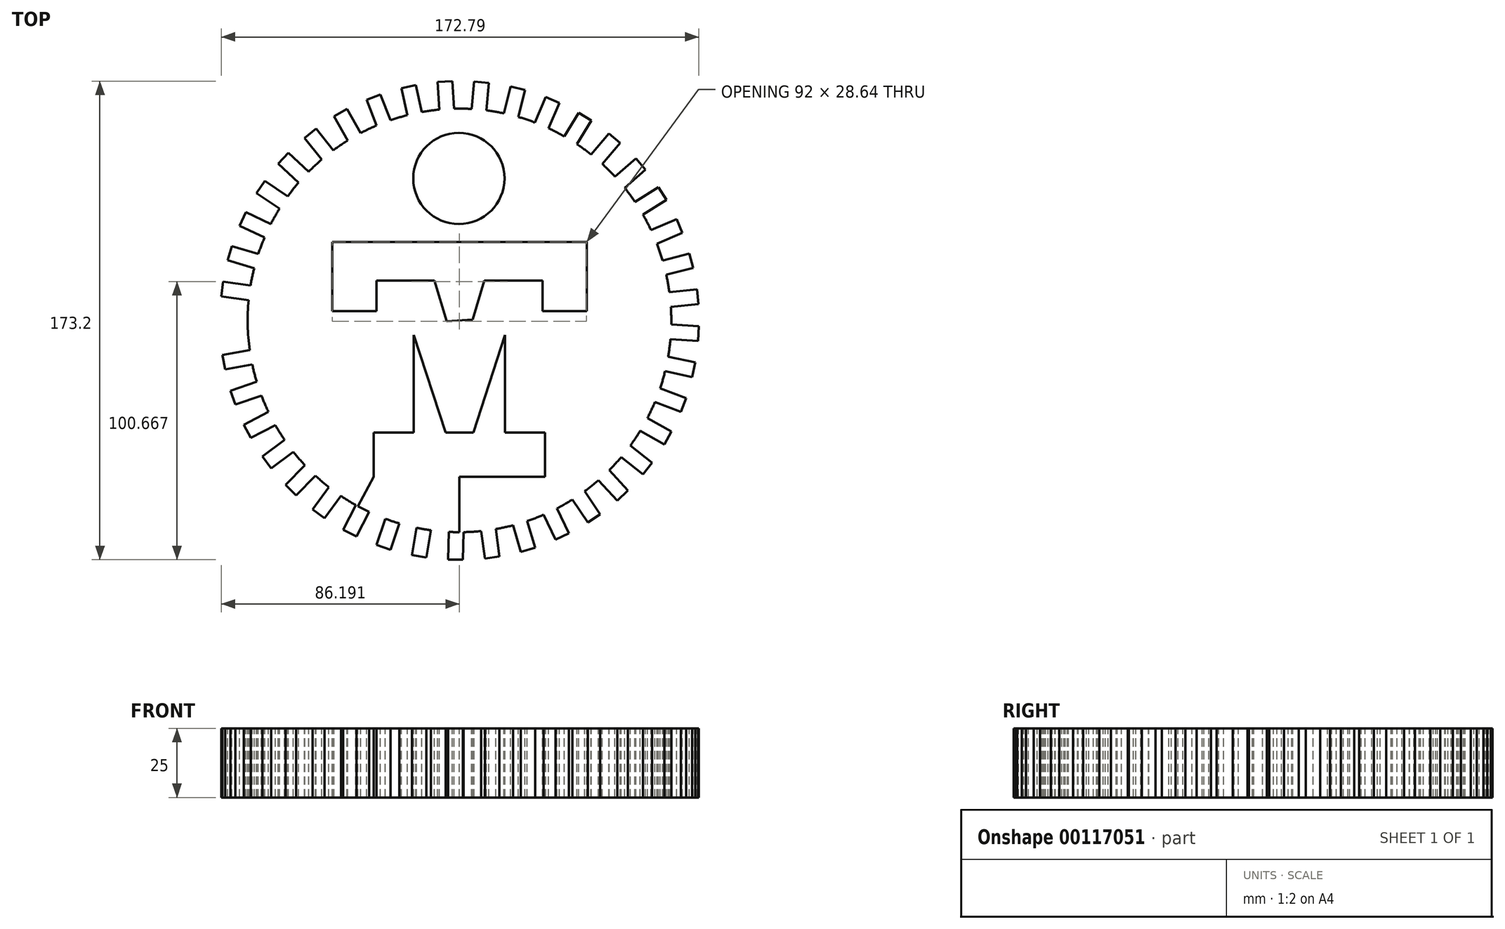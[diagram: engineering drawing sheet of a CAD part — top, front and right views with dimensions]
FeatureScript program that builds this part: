
annotation { "Feature Type Name" : "Feature", "Feature Type Description" : "" }
export const myFeature = defineFeature(function(context is Context, id is Id, definition is map)
    precondition{}
    {
        {
            var Q0;
            Q0=qCreatedBy(makeId("Top.planeOp"),FACE);
            var sketch = newSketch(context, id + "F0", { "sketchPlane" : qUnion([Q0])});
            skLineSegment(sketch, "E0", {"start": v(-32.27, 42.96) * mm, "end": v(-32.27, 17.96) * mm});
            skLineSegment(sketch, "E1", {"start": v(-32.27, 42.96) * mm, "end": v(59.73, 42.96) * mm});
            skLineSegment(sketch, "E2", {"start": v(59.73, 42.96) * mm, "end": v(59.73, 17.96) * mm});
            skLineSegment(sketch, "E3", {"start": v(59.73, 17.96) * mm, "end": v(43.73, 17.96) * mm});
            skLineSegment(sketch, "E4", {"start": v(43.73, 17.96) * mm, "end": v(43.73, 28.96) * mm});
            skLineSegment(sketch, "E5", {"start": v(43.73, 28.96) * mm, "end": v(22.73, 28.96) * mm});
            skLineSegment(sketch, "E6", {"start": v(22.73, 28.96) * mm, "end": v(13.73, -1.04) * mm});
            skLineSegment(sketch, "E7", {"start": v(13.73, -1.04) * mm, "end": v(4.73, 28.96) * mm});
            skLineSegment(sketch, "E8", {"start": v(4.73, 28.96) * mm, "end": v(-16.27, 28.96) * mm});
            skLineSegment(sketch, "E9", {"start": v(-16.27, 28.96) * mm, "end": v(-16.27, 17.96) * mm});
            skLineSegment(sketch, "E10", {"start": v(-16.27, 17.96) * mm, "end": v(-32.27, 17.96) * mm});
            skLineSegment(sketch, "E11", {"start": v(-2.77, 9.26) * mm, "end": v(-2.77, -26.04) * mm});
            skLineSegment(sketch, "E12", {"start": v(-2.77, -26.04) * mm, "end": v(-17.27, -26.04) * mm});
            skLineSegment(sketch, "E13", {"start": v(-17.27, -26.04) * mm, "end": v(-17.27, -42.04) * mm});
            skLineSegment(sketch, "E14", {"start": v(-17.27, -42.04) * mm, "end": v(44.73, -42.04) * mm});
            skLineSegment(sketch, "E15", {"start": v(44.73, -42.04) * mm, "end": v(44.73, -26.04) * mm});
            skLineSegment(sketch, "E16", {"start": v(44.73, -26.04) * mm, "end": v(30.23, -26.04) * mm});
            skLineSegment(sketch, "E17", {"start": v(30.23, -26.04) * mm, "end": v(30.23, 9.26) * mm});
            skLineSegment(sketch, "E18", {"start": v(30.23, 9.26) * mm, "end": v(18.73, -26.04) * mm});
            skLineSegment(sketch, "E19", {"start": v(18.73, -26.04) * mm, "end": v(8.73, -26.04) * mm});
            skLineSegment(sketch, "E20", {"start": v(8.73, -26.04) * mm, "end": v(-2.77, 9.26) * mm});
            skCircle(sketch, "E21", {"center": v(13.52, 65.96) * mm, "radius": 16.5 * mm});
            skLineSegment(sketch, "E22", {"start": v(13.73, -1.04) * mm, "end": v(13.73, -42.04) * mm});
            skCircle(sketch, "E23", {"center": v(13.73, 14.58) * mm, "radius": 76.63 * mm});
            skLineSegment(sketch, "E24", {"start": v(13.73, 14.58) * mm, "end": v(13.73, 42.96) * mm});
            skPoint(sketch, "E24.endSnap0", {"position": v(13.73, 42.96) * mm});
            skLineSegment(sketch, "E25", {"start": v(13.73, -62.04) * mm, "end": v(13.73, -42.04) * mm});
            skPoint(sketch, "E26", {"position": v(-62.74, 19.53) * mm});
            skPoint(sketch, "E27", {"position": v(-62.08, 3.44) * mm});
            skLineSegment(sketch, "E28", {"start": v(13.73, 14.58) * mm, "end": v(9.12, 14.32) * mm});
            skLineSegment(sketch, "E29", {"start": v(-62.77, 10.21) * mm, "end": v(-72.77, 10) * mm});
            skLineSegment(sketch, "E30", {"start": v(-72.77, 10) * mm, "end": v(-72.89, 15.34) * mm});
            skLineSegment(sketch, "E31", {"start": v(-72.89, 15.34) * mm, "end": v(-62.89, 15.56) * mm});
            skLineSegment(sketch, "E32", {"start": v(-62.89, 15.56) * mm, "end": v(-62.77, 10.21) * mm});
            skLineSegment(sketch, "E33.1.0", {"start": v(-72.46, 23.25) * mm, "end": v(-71.76, 28.55) * mm});
            skLineSegment(sketch, "E33.1.1", {"start": v(-71.76, 28.55) * mm, "end": v(-61.84, 27.24) * mm});
            skLineSegment(sketch, "E33.1.2", {"start": v(-62.54, 21.94) * mm, "end": v(-72.46, 23.25) * mm});
            skPoint(sketch, "E33.1.3", {"position": v(-62.9, 15.15) * mm});
            skLineSegment(sketch, "E33.2.0", {"start": v(-70.13, 36.3) * mm, "end": v(-68.63, 41.44) * mm});
            skLineSegment(sketch, "E33.2.1", {"start": v(-68.63, 41.44) * mm, "end": v(-59.02, 38.63) * mm});
            skLineSegment(sketch, "E33.2.2", {"start": v(-60.52, 33.5) * mm, "end": v(-70.13, 36.3) * mm});
            skPoint(sketch, "E33.2.3", {"position": v(-61.91, 26.84) * mm});
            skLineSegment(sketch, "E33.3.0", {"start": v(-65.83, 48.85) * mm, "end": v(-63.56, 53.7) * mm});
            skLineSegment(sketch, "E33.3.1", {"start": v(-63.56, 53.7) * mm, "end": v(-54.5, 49.46) * mm});
            skLineSegment(sketch, "E33.3.2", {"start": v(-56.77, 44.61) * mm, "end": v(-65.83, 48.85) * mm});
            skPoint(sketch, "E33.3.3", {"position": v(-59.15, 38.24) * mm});
            skLineSegment(sketch, "E33.4.0", {"start": v(-59.66, 60.6) * mm, "end": v(-56.68, 65.04) * mm});
            skLineSegment(sketch, "E33.4.1", {"start": v(-56.68, 65.04) * mm, "end": v(-48.38, 59.46) * mm});
            skLineSegment(sketch, "E33.4.2", {"start": v(-51.36, 55.02) * mm, "end": v(-59.66, 60.6) * mm});
            skPoint(sketch, "E33.4.3", {"position": v(-54.69, 49.09) * mm});
            skLineSegment(sketch, "E33.5.0", {"start": v(-51.78, 71.26) * mm, "end": v(-48.16, 75.2) * mm});
            skLineSegment(sketch, "E33.5.1", {"start": v(-48.16, 75.2) * mm, "end": v(-40.8, 68.42) * mm});
            skLineSegment(sketch, "E33.5.2", {"start": v(-44.42, 64.48) * mm, "end": v(-51.78, 71.26) * mm});
            skPoint(sketch, "E33.5.3", {"position": v(-48.62, 59.13) * mm});
            skLineSegment(sketch, "E33.6.0", {"start": v(-42.36, 80.6) * mm, "end": v(-38.18, 83.93) * mm});
            skLineSegment(sketch, "E33.6.1", {"start": v(-38.18, 83.93) * mm, "end": v(-31.94, 76.11) * mm});
            skLineSegment(sketch, "E33.6.2", {"start": v(-36.12, 72.78) * mm, "end": v(-42.36, 80.6) * mm});
            skPoint(sketch, "E33.6.3", {"position": v(-41.09, 68.12) * mm});
            skLineSegment(sketch, "E33.7.0", {"start": v(-31.63, 88.38) * mm, "end": v(-26.99, 91.04) * mm});
            skLineSegment(sketch, "E33.7.1", {"start": v(-26.99, 91.04) * mm, "end": v(-22.01, 82.36) * mm});
            skLineSegment(sketch, "E33.7.2", {"start": v(-26.65, 79.7) * mm, "end": v(-31.63, 88.38) * mm});
            skPoint(sketch, "E33.7.3", {"position": v(-32.27, 75.86) * mm});
            skLineSegment(sketch, "E33.8.0", {"start": v(-19.83, 94.44) * mm, "end": v(-14.84, 96.36) * mm});
            skLineSegment(sketch, "E33.8.1", {"start": v(-14.84, 96.36) * mm, "end": v(-11.25, 87.02) * mm});
            skLineSegment(sketch, "E33.8.2", {"start": v(-16.24, 85.1) * mm, "end": v(-19.83, 94.44) * mm});
            skPoint(sketch, "E33.8.3", {"position": v(-22.38, 82.17) * mm});
            skLineSegment(sketch, "E33.9.0", {"start": v(-7.25, 98.63) * mm, "end": v(-2.02, 99.76) * mm});
            skLineSegment(sketch, "E33.9.1", {"start": v(-2.02, 99.76) * mm, "end": v(0.1, 89.99) * mm});
            skLineSegment(sketch, "E33.9.2", {"start": v(-5.12, 88.85) * mm, "end": v(-7.25, 98.63) * mm});
            skPoint(sketch, "E33.9.3", {"position": v(-11.64, 86.89) * mm});
            skLineSegment(sketch, "E33.10.0", {"start": v(5.83, 100.85) * mm, "end": v(11.17, 101.17) * mm});
            skLineSegment(sketch, "E33.10.1", {"start": v(11.17, 101.17) * mm, "end": v(11.77, 91.18) * mm});
            skLineSegment(sketch, "E33.10.2", {"start": v(6.43, 90.86) * mm, "end": v(5.83, 100.85) * mm});
            skPoint(sketch, "E33.10.3", {"position": v(-0.3, 89.91) * mm});
            skLineSegment(sketch, "E33.11.0", {"start": v(19.1, 101.04) * mm, "end": v(24.42, 100.54) * mm});
            skLineSegment(sketch, "E33.11.1", {"start": v(24.42, 100.54) * mm, "end": v(23.49, 90.59) * mm});
            skLineSegment(sketch, "E33.11.2", {"start": v(18.16, 91.08) * mm, "end": v(19.1, 101.04) * mm});
            skPoint(sketch, "E33.11.3", {"position": v(11.36, 91.17) * mm});
            skLineSegment(sketch, "E33.12.0", {"start": v(32.23, 99.2) * mm, "end": v(37.41, 97.9) * mm});
            skLineSegment(sketch, "E33.12.1", {"start": v(37.41, 97.9) * mm, "end": v(34.98, 88.2) * mm});
            skLineSegment(sketch, "E33.12.2", {"start": v(29.79, 89.5) * mm, "end": v(32.23, 99.2) * mm});
            skPoint(sketch, "E33.12.3", {"position": v(23.08, 90.64) * mm});
            skLineSegment(sketch, "E33.13.0", {"start": v(44.93, 95.4) * mm, "end": v(49.85, 93.31) * mm});
            skLineSegment(sketch, "E33.13.1", {"start": v(49.85, 93.31) * mm, "end": v(45.97, 84.1) * mm});
            skLineSegment(sketch, "E33.13.2", {"start": v(41.04, 86.18) * mm, "end": v(44.93, 95.4) * mm});
            skPoint(sketch, "E33.13.3", {"position": v(34.58, 88.32) * mm});
            skLineSegment(sketch, "E33.14.0", {"start": v(56.9, 89.69) * mm, "end": v(61.45, 86.88) * mm});
            skLineSegment(sketch, "E33.14.1", {"start": v(61.45, 86.88) * mm, "end": v(56.2, 78.36) * mm});
            skLineSegment(sketch, "E33.14.2", {"start": v(51.65, 81.17) * mm, "end": v(56.9, 89.69) * mm});
            skPoint(sketch, "E33.14.3", {"position": v(45.6, 84.27) * mm});
            skLineSegment(sketch, "E33.15.0", {"start": v(67.86, 82.22) * mm, "end": v(71.93, 78.75) * mm});
            skLineSegment(sketch, "E33.15.1", {"start": v(71.93, 78.75) * mm, "end": v(65.44, 71.13) * mm});
            skLineSegment(sketch, "E33.15.2", {"start": v(61.37, 74.6) * mm, "end": v(67.86, 82.22) * mm});
            skPoint(sketch, "E33.15.3", {"position": v(55.86, 78.6) * mm});
            skLineSegment(sketch, "E33.16.0", {"start": v(77.55, 73.16) * mm, "end": v(81.04, 69.11) * mm});
            skLineSegment(sketch, "E33.16.1", {"start": v(81.04, 69.11) * mm, "end": v(73.46, 62.58) * mm});
            skLineSegment(sketch, "E33.16.2", {"start": v(69.97, 66.63) * mm, "end": v(77.55, 73.16) * mm});
            skPoint(sketch, "E33.16.3", {"position": v(65.13, 71.41) * mm});
            skLineSegment(sketch, "E33.17.0", {"start": v(85.74, 62.73) * mm, "end": v(88.57, 58.2) * mm});
            skLineSegment(sketch, "E33.17.1", {"start": v(88.57, 58.2) * mm, "end": v(80.1, 52.9) * mm});
            skLineSegment(sketch, "E33.17.2", {"start": v(77.26, 57.43) * mm, "end": v(85.74, 62.73) * mm});
            skPoint(sketch, "E33.17.3", {"position": v(73.2, 62.9) * mm});
            skLineSegment(sketch, "E33.18.0", {"start": v(92.25, 51.18) * mm, "end": v(94.35, 46.26) * mm});
            skLineSegment(sketch, "E33.18.1", {"start": v(94.35, 46.26) * mm, "end": v(85.16, 42.32) * mm});
            skLineSegment(sketch, "E33.18.2", {"start": v(83.05, 47.23) * mm, "end": v(92.25, 51.18) * mm});
            skPoint(sketch, "E33.18.3", {"position": v(79.88, 53.25) * mm});
            skLineSegment(sketch, "E33.19.0", {"start": v(96.91, 38.76) * mm, "end": v(98.25, 33.58) * mm});
            skLineSegment(sketch, "E33.19.1", {"start": v(98.25, 33.58) * mm, "end": v(88.56, 31.09) * mm});
            skLineSegment(sketch, "E33.19.2", {"start": v(87.23, 36.27) * mm, "end": v(96.91, 38.76) * mm});
            skPoint(sketch, "E33.19.3", {"position": v(85.01, 42.7) * mm});
            skLineSegment(sketch, "E33.20.0", {"start": v(99.63, 25.78) * mm, "end": v(100.16, 20.46) * mm});
            skLineSegment(sketch, "E33.20.1", {"start": v(100.16, 20.46) * mm, "end": v(90.2, 19.47) * mm});
            skLineSegment(sketch, "E33.20.2", {"start": v(89.67, 24.8) * mm, "end": v(99.63, 25.78) * mm});
            skPoint(sketch, "E33.20.3", {"position": v(88.47, 31.5) * mm});
            skLineSegment(sketch, "E33.21.0", {"start": v(100.33, 12.54) * mm, "end": v(100.04, 7.2) * mm});
            skLineSegment(sketch, "E33.21.1", {"start": v(100.04, 7.2) * mm, "end": v(90.05, 7.74) * mm});
            skLineSegment(sketch, "E33.21.2", {"start": v(90.34, 13.08) * mm, "end": v(100.33, 12.54) * mm});
            skPoint(sketch, "E33.21.3", {"position": v(90.17, 19.89) * mm});
            skLineSegment(sketch, "E33.22.0", {"start": v(99, -0.66) * mm, "end": v(97.9, -5.9) * mm});
            skLineSegment(sketch, "E33.22.1", {"start": v(97.9, -5.9) * mm, "end": v(88.11, -3.83) * mm});
            skLineSegment(sketch, "E33.22.2", {"start": v(89.22, 1.4) * mm, "end": v(99, -0.66) * mm});
            skPoint(sketch, "E33.22.3", {"position": v(90.09, 8.15) * mm});
            skLineSegment(sketch, "E33.23.0", {"start": v(95.68, -13.5) * mm, "end": v(93.79, -18.5) * mm});
            skLineSegment(sketch, "E33.23.1", {"start": v(93.79, -18.5) * mm, "end": v(84.43, -14.97) * mm});
            skLineSegment(sketch, "E33.23.2", {"start": v(86.32, -9.96) * mm, "end": v(95.68, -13.5) * mm});
            skPoint(sketch, "E33.23.3", {"position": v(88.21, -3.43) * mm});
            skLineSegment(sketch, "E33.24.0", {"start": v(90.43, -25.68) * mm, "end": v(87.8, -30.33) * mm});
            skLineSegment(sketch, "E33.24.1", {"start": v(87.8, -30.33) * mm, "end": v(79.1, -25.41) * mm});
            skLineSegment(sketch, "E33.24.2", {"start": v(81.72, -20.76) * mm, "end": v(90.43, -25.68) * mm});
            skPoint(sketch, "E33.24.3", {"position": v(84.59, -14.58) * mm});
            skLineSegment(sketch, "E33.25.0", {"start": v(83.39, -36.91) * mm, "end": v(80.08, -41.11) * mm});
            skLineSegment(sketch, "E33.25.1", {"start": v(80.08, -41.11) * mm, "end": v(72.22, -34.92) * mm});
            skLineSegment(sketch, "E33.25.2", {"start": v(75.53, -30.72) * mm, "end": v(83.39, -36.91) * mm});
            skPoint(sketch, "E33.25.3", {"position": v(79.3, -25.06) * mm});
            skLineSegment(sketch, "E33.26.0", {"start": v(74.71, -46.94) * mm, "end": v(70.8, -50.59) * mm});
            skLineSegment(sketch, "E33.26.1", {"start": v(70.8, -50.59) * mm, "end": v(63.98, -43.27) * mm});
            skLineSegment(sketch, "E33.26.2", {"start": v(67.9, -39.62) * mm, "end": v(74.71, -46.94) * mm});
            skPoint(sketch, "E33.26.3", {"position": v(72.49, -34.6) * mm});
            skLineSegment(sketch, "E33.27.0", {"start": v(64.6, -55.53) * mm, "end": v(60.18, -58.54) * mm});
            skLineSegment(sketch, "E33.27.1", {"start": v(60.18, -58.54) * mm, "end": v(54.56, -50.26) * mm});
            skLineSegment(sketch, "E33.27.2", {"start": v(58.98, -47.26) * mm, "end": v(64.6, -55.53) * mm});
            skPoint(sketch, "E33.27.3", {"position": v(64.3, -43) * mm});
            skLineSegment(sketch, "E33.28.0", {"start": v(53.3, -62.47) * mm, "end": v(48.48, -64.77) * mm});
            skLineSegment(sketch, "E33.28.1", {"start": v(48.48, -64.77) * mm, "end": v(44.18, -55.73) * mm});
            skLineSegment(sketch, "E33.28.2", {"start": v(49.01, -53.44) * mm, "end": v(53.3, -62.47) * mm});
            skPoint(sketch, "E33.28.3", {"position": v(54.9, -50.04) * mm});
            skLineSegment(sketch, "E33.29.0", {"start": v(41.08, -67.61) * mm, "end": v(35.95, -69.14) * mm});
            skLineSegment(sketch, "E33.29.1", {"start": v(35.95, -69.14) * mm, "end": v(33.1, -59.56) * mm});
            skLineSegment(sketch, "E33.29.2", {"start": v(38.22, -58.03) * mm, "end": v(41.08, -67.61) * mm});
            skPoint(sketch, "E33.29.3", {"position": v(44.56, -55.57) * mm});
            skLineSegment(sketch, "E33.30.0", {"start": v(28.21, -70.82) * mm, "end": v(22.91, -71.55) * mm});
            skLineSegment(sketch, "E33.30.1", {"start": v(22.91, -71.55) * mm, "end": v(21.55, -61.65) * mm});
            skLineSegment(sketch, "E33.30.2", {"start": v(26.85, -60.91) * mm, "end": v(28.21, -70.82) * mm});
            skPoint(sketch, "E33.30.3", {"position": v(33.5, -59.45) * mm});
            skLineSegment(sketch, "E33.31.0", {"start": v(15, -72.03) * mm, "end": v(9.66, -71.95) * mm});
            skLineSegment(sketch, "E33.31.1", {"start": v(9.66, -71.95) * mm, "end": v(9.82, -61.94) * mm});
            skLineSegment(sketch, "E33.31.2", {"start": v(15.17, -62.03) * mm, "end": v(15, -72.03) * mm});
            skPoint(sketch, "E33.31.3", {"position": v(21.96, -61.6) * mm});
            skLineSegment(sketch, "E33.32.0", {"start": v(1.77, -71.21) * mm, "end": v(-3.5, -70.31) * mm});
            skLineSegment(sketch, "E33.32.1", {"start": v(-3.5, -70.31) * mm, "end": v(-1.82, -60.45) * mm});
            skLineSegment(sketch, "E33.32.2", {"start": v(3.46, -61.35) * mm, "end": v(1.77, -71.21) * mm});
            skPoint(sketch, "E33.32.3", {"position": v(10.23, -61.96) * mm});
            skLineSegment(sketch, "E33.33.0", {"start": v(-11.19, -68.38) * mm, "end": v(-16.26, -66.68) * mm});
            skLineSegment(sketch, "E33.33.1", {"start": v(-16.26, -66.68) * mm, "end": v(-13.09, -57.2) * mm});
            skLineSegment(sketch, "E33.33.2", {"start": v(-8.02, -58.9) * mm, "end": v(-11.19, -68.38) * mm});
            skPoint(sketch, "E33.33.3", {"position": v(-1.41, -60.53) * mm});
            skLineSegment(sketch, "E33.34.0", {"start": v(-23.56, -63.6) * mm, "end": v(-28.31, -61.15) * mm});
            skLineSegment(sketch, "E33.34.1", {"start": v(-28.31, -61.15) * mm, "end": v(-23.73, -52.26) * mm});
            skLineSegment(sketch, "E33.34.2", {"start": v(-18.98, -54.71) * mm, "end": v(-23.56, -63.6) * mm});
            skPoint(sketch, "E33.34.3", {"position": v(-12.7, -57.34) * mm});
            skLineSegment(sketch, "E33.35.0", {"start": v(-35.06, -57) * mm, "end": v(-39.38, -53.85) * mm});
            skLineSegment(sketch, "E33.35.1", {"start": v(-39.38, -53.85) * mm, "end": v(-33.5, -45.76) * mm});
            skLineSegment(sketch, "E33.35.2", {"start": v(-29.17, -48.9) * mm, "end": v(-35.06, -57) * mm});
            skPoint(sketch, "E33.35.3", {"position": v(-23.37, -52.46) * mm});
            skLineSegment(sketch, "E33.36.0", {"start": v(-45.41, -48.7) * mm, "end": v(-49.2, -44.94) * mm});
            skLineSegment(sketch, "E33.36.1", {"start": v(-49.2, -44.94) * mm, "end": v(-42.15, -37.84) * mm});
            skLineSegment(sketch, "E33.36.2", {"start": v(-38.36, -41.62) * mm, "end": v(-45.41, -48.7) * mm});
            skPoint(sketch, "E33.36.3", {"position": v(-33.17, -46.02) * mm});
            skLineSegment(sketch, "E33.37.0", {"start": v(-54.38, -38.94) * mm, "end": v(-57.55, -34.63) * mm});
            skLineSegment(sketch, "E33.37.1", {"start": v(-57.55, -34.63) * mm, "end": v(-49.5, -28.7) * mm});
            skLineSegment(sketch, "E33.37.2", {"start": v(-46.33, -33) * mm, "end": v(-54.38, -38.94) * mm});
            skPoint(sketch, "E33.37.3", {"position": v(-41.87, -38.15) * mm});
            skLineSegment(sketch, "E33.38.0", {"start": v(-61.75, -27.92) * mm, "end": v(-64.23, -23.18) * mm});
            skLineSegment(sketch, "E33.38.1", {"start": v(-64.23, -23.18) * mm, "end": v(-55.37, -18.54) * mm});
            skLineSegment(sketch, "E33.38.2", {"start": v(-52.89, -23.28) * mm, "end": v(-61.75, -27.92) * mm});
            skPoint(sketch, "E33.38.3", {"position": v(-49.27, -29.04) * mm});
            skLineSegment(sketch, "E33.39.0", {"start": v(-67.35, -15.9) * mm, "end": v(-69.08, -10.83) * mm});
            skLineSegment(sketch, "E33.39.1", {"start": v(-69.08, -10.83) * mm, "end": v(-59.61, -7.6) * mm});
            skLineSegment(sketch, "E33.39.2", {"start": v(-57.89, -12.67) * mm, "end": v(-67.35, -15.9) * mm});
            skPoint(sketch, "E33.39.3", {"position": v(-55.19, -18.91) * mm});
            skLineSegment(sketch, "E33.40.0", {"start": v(-71.06, -3.16) * mm, "end": v(-72, 2.1) * mm});
            skLineSegment(sketch, "E33.40.1", {"start": v(-72, 2.1) * mm, "end": v(-62.14, 3.85) * mm});
            skLineSegment(sketch, "E33.40.2", {"start": v(-61.2, -1.41) * mm, "end": v(-71.06, -3.16) * mm});
            skPoint(sketch, "E33.40.3", {"position": v(-59.5, -8) * mm});
            skLineSegment(sketch, "E33.anchor1", {"start": v(13.73, 14.58) * mm, "end": v(-72.77, 10) * mm, "construction": true});
            skLineSegment(sketch, "E33.anchor2", {"start": v(13.73, 14.58) * mm, "end": v(-72.77, 10) * mm, "construction": true});
            skLineSegment(sketch, "E34.trimOffspring", {"start": v(13.73, 49.46) * mm, "end": v(13.73, 82.45) * mm});
            skPoint(sketch, "E35.orphan", {"position": v(13.73, 91.2) * mm});
            skLineSegment(sketch, "E36.trimOffspring", {"start": v(72.78, 17.96) * mm, "end": v(-16.27, 12.87) * mm});
            skArc(sketch, "E37", {"start": v(-69.08, -10.83) * mm, "mid": v(-75.61, -6.16) * mm, "end": v(-82.15, -10.83) * mm});
            skLineSegment(sketch, "E38", {"start": v(-17.27, -42.04) * mm, "end": v(-23.07, -52.63) * mm});
            skLineSegment(sketch, "E39", {"start": v(13.73, 82.45) * mm, "end": v(13.73, 91.2) * mm});
            skSolve(sketch);
        }
        {
            var Q0;
            {var subQ81=sQuery(id+"F0.wireOp",EDGE,"E0");Q0=makeQuery(id+"F0.imprint","IMPRINT",FACE,{"disambiguationData":[TD([[makeQuery(id+"F0.imprint","IMPRINT",EDGE,{"derivedFrom":subQ81}),-1.0]])]});}
            var Q1;
            {var subQ3=sQuery(id+"F0.wireOp",EDGE,"E36.trimOffspring");Q1=makeQuery(id+"F0.imprint","IMPRINT",FACE,{"disambiguationData":[TD([[makeQuery(id+"F0.imprint","IMPRINT",EDGE,{"derivedFrom":subQ3}),1.0]])]});}
            var Q2;
            Q2=makeQuery(id+"F0.imprint","IMPRINT",FACE,{"disambiguationData":[TD([[makeQuery(id+"F0.imprint","IMPRINT",EDGE,{"derivedFrom":sQuery(id+"F0.wireOp",EDGE,"E33.35.0")}),-1.0]])]});
            var Q3;
            Q3=makeQuery(id+"F0.imprint","IMPRINT",FACE,{"disambiguationData":[TD([[makeQuery(id+"F0.imprint","IMPRINT",EDGE,{"derivedFrom":sQuery(id+"F0.wireOp",EDGE,"E33.33.0")}),-1.0]])]});
            var Q4;
            Q4=makeQuery(id+"F0.imprint","IMPRINT",FACE,{"disambiguationData":[TD([[makeQuery(id+"F0.imprint","IMPRINT",EDGE,{"derivedFrom":sQuery(id+"F0.wireOp",EDGE,"E33.6.0")}),-1.0]])]});
            var Q5;
            Q5=makeQuery(id+"F0.imprint","IMPRINT",FACE,{"disambiguationData":[TD([[makeQuery(id+"F0.imprint","IMPRINT",EDGE,{"derivedFrom":sQuery(id+"F0.wireOp",EDGE,"E33.19.0")}),-1.0]])]});
            var Q6;
            Q6=makeQuery(id+"F0.imprint","IMPRINT",FACE,{"disambiguationData":[TD([[makeQuery(id+"F0.imprint","IMPRINT",EDGE,{"derivedFrom":sQuery(id+"F0.wireOp",EDGE,"E33.18.0")}),-1.0]])]});
            var Q7;
            Q7=makeQuery(id+"F0.imprint","IMPRINT",FACE,{"disambiguationData":[TD([[makeQuery(id+"F0.imprint","IMPRINT",EDGE,{"derivedFrom":sQuery(id+"F0.wireOp",EDGE,"E33.17.0")}),-1.0]])]});
            var Q8;
            Q8=makeQuery(id+"F0.imprint","IMPRINT",FACE,{"disambiguationData":[TD([[makeQuery(id+"F0.imprint","IMPRINT",EDGE,{"derivedFrom":sQuery(id+"F0.wireOp",EDGE,"E33.16.0")}),-1.0]])]});
            var Q9;
            Q9=makeQuery(id+"F0.imprint","IMPRINT",FACE,{"disambiguationData":[TD([[makeQuery(id+"F0.imprint","IMPRINT",EDGE,{"derivedFrom":sQuery(id+"F0.wireOp",EDGE,"E33.15.0")}),-1.0]])]});
            var Q10;
            Q10=makeQuery(id+"F0.imprint","IMPRINT",FACE,{"disambiguationData":[TD([[makeQuery(id+"F0.imprint","IMPRINT",EDGE,{"derivedFrom":sQuery(id+"F0.wireOp",EDGE,"E33.14.0")}),-1.0]])]});
            var Q11;
            Q11=makeQuery(id+"F0.imprint","IMPRINT",FACE,{"disambiguationData":[TD([[makeQuery(id+"F0.imprint","IMPRINT",EDGE,{"derivedFrom":sQuery(id+"F0.wireOp",EDGE,"E33.13.0")}),-1.0]])]});
            var Q12;
            Q12=makeQuery(id+"F0.imprint","IMPRINT",FACE,{"disambiguationData":[TD([[makeQuery(id+"F0.imprint","IMPRINT",EDGE,{"derivedFrom":sQuery(id+"F0.wireOp",EDGE,"E33.12.0")}),-1.0]])]});
            var Q13;
            Q13=makeQuery(id+"F0.imprint","IMPRINT",FACE,{"disambiguationData":[TD([[makeQuery(id+"F0.imprint","IMPRINT",EDGE,{"derivedFrom":sQuery(id+"F0.wireOp",EDGE,"E33.10.0")}),-1.0]])]});
            var Q14;
            Q14=makeQuery(id+"F0.imprint","IMPRINT",FACE,{"disambiguationData":[TD([[makeQuery(id+"F0.imprint","IMPRINT",EDGE,{"derivedFrom":sQuery(id+"F0.wireOp",EDGE,"E33.22.0")}),-1.0]])]});
            var Q15;
            Q15=makeQuery(id+"F0.imprint","IMPRINT",FACE,{"disambiguationData":[TD([[makeQuery(id+"F0.imprint","IMPRINT",EDGE,{"derivedFrom":sQuery(id+"F0.wireOp",EDGE,"E33.38.0")}),-1.0]])]});
            var Q16;
            Q16=makeQuery(id+"F0.imprint","IMPRINT",FACE,{"disambiguationData":[TD([[makeQuery(id+"F0.imprint","IMPRINT",EDGE,{"derivedFrom":sQuery(id+"F0.wireOp",EDGE,"E33.21.0")}),-1.0]])]});
            var Q17;
            Q17=makeQuery(id+"F0.imprint","IMPRINT",FACE,{"disambiguationData":[TD([[makeQuery(id+"F0.imprint","IMPRINT",EDGE,{"derivedFrom":sQuery(id+"F0.wireOp",EDGE,"E33.37.0")}),-1.0]])]});
            var Q18;
            Q18=makeQuery(id+"F0.imprint","IMPRINT",FACE,{"disambiguationData":[TD([[makeQuery(id+"F0.imprint","IMPRINT",EDGE,{"derivedFrom":sQuery(id+"F0.wireOp",EDGE,"E33.36.0")}),-1.0]])]});
            var Q19;
            Q19=makeQuery(id+"F0.imprint","IMPRINT",FACE,{"disambiguationData":[TD([[makeQuery(id+"F0.imprint","IMPRINT",EDGE,{"derivedFrom":sQuery(id+"F0.wireOp",EDGE,"E33.32.0")}),-1.0]])]});
            var Q20;
            Q20=makeQuery(id+"F0.imprint","IMPRINT",FACE,{"disambiguationData":[TD([[makeQuery(id+"F0.imprint","IMPRINT",EDGE,{"derivedFrom":sQuery(id+"F0.wireOp",EDGE,"E33.34.0")}),-1.0]])]});
            var Q21;
            Q21=makeQuery(id+"F0.imprint","IMPRINT",FACE,{"disambiguationData":[TD([[makeQuery(id+"F0.imprint","IMPRINT",EDGE,{"derivedFrom":sQuery(id+"F0.wireOp",EDGE,"E33.4.0")}),-1.0]])]});
            var Q22;
            Q22=makeQuery(id+"F0.imprint","IMPRINT",FACE,{"disambiguationData":[TD([[makeQuery(id+"F0.imprint","IMPRINT",EDGE,{"derivedFrom":sQuery(id+"F0.wireOp",EDGE,"E33.3.0")}),-1.0]])]});
            var Q23;
            Q23=makeQuery(id+"F0.imprint","IMPRINT",FACE,{"disambiguationData":[TD([[makeQuery(id+"F0.imprint","IMPRINT",EDGE,{"derivedFrom":sQuery(id+"F0.wireOp",EDGE,"E33.2.0")}),-1.0]])]});
            var Q24;
            Q24=makeQuery(id+"F0.imprint","IMPRINT",FACE,{"disambiguationData":[TD([[makeQuery(id+"F0.imprint","IMPRINT",EDGE,{"derivedFrom":sQuery(id+"F0.wireOp",EDGE,"E33.27.0")}),-1.0]])]});
            var Q25;
            Q25=makeQuery(id+"F0.imprint","IMPRINT",FACE,{"disambiguationData":[TD([[makeQuery(id+"F0.imprint","IMPRINT",EDGE,{"derivedFrom":sQuery(id+"F0.wireOp",EDGE,"E33.1.0")}),-1.0]])]});
            var Q26;
            Q26=makeQuery(id+"F0.imprint","IMPRINT",FACE,{"disambiguationData":[TD([[makeQuery(id+"F0.imprint","IMPRINT",EDGE,{"derivedFrom":sQuery(id+"F0.wireOp",EDGE,"E33.25.0")}),-1.0]])]});
            var Q27;
            Q27=makeQuery(id+"F0.imprint","IMPRINT",FACE,{"disambiguationData":[TD([[makeQuery(id+"F0.imprint","IMPRINT",EDGE,{"derivedFrom":sQuery(id+"F0.wireOp",EDGE,"E33.40.0")}),-1.0]])]});
            var Q28;
            Q28=makeQuery(id+"F0.imprint","IMPRINT",FACE,{"disambiguationData":[TD([[makeQuery(id+"F0.imprint","IMPRINT",EDGE,{"derivedFrom":sQuery(id+"F0.wireOp",EDGE,"E33.24.0")}),-1.0]])]});
            var Q29;
            Q29=makeQuery(id+"F0.imprint","IMPRINT",FACE,{"disambiguationData":[TD([[makeQuery(id+"F0.imprint","IMPRINT",EDGE,{"derivedFrom":sQuery(id+"F0.wireOp",EDGE,"E33.23.0")}),-1.0]])]});
            var Q30;
            Q30=makeQuery(id+"F0.imprint","IMPRINT",FACE,{"disambiguationData":[TD([[makeQuery(id+"F0.imprint","IMPRINT",EDGE,{"derivedFrom":sQuery(id+"F0.wireOp",EDGE,"E33.39.0")}),-1.0]])]});
            var Q31;
            Q31=makeQuery(id+"F0.imprint","IMPRINT",FACE,{"disambiguationData":[TD([[makeQuery(id+"F0.imprint","IMPRINT",EDGE,{"derivedFrom":sQuery(id+"F0.wireOp",EDGE,"E33.5.0")}),-1.0]])]});
            var Q32;
            Q32=makeQuery(id+"F0.imprint","IMPRINT",FACE,{"disambiguationData":[TD([[makeQuery(id+"F0.imprint","IMPRINT",EDGE,{"derivedFrom":sQuery(id+"F0.wireOp",EDGE,"E33.7.0")}),-1.0]])]});
            var Q33;
            Q33=makeQuery(id+"F0.imprint","IMPRINT",FACE,{"disambiguationData":[TD([[makeQuery(id+"F0.imprint","IMPRINT",EDGE,{"derivedFrom":sQuery(id+"F0.wireOp",EDGE,"E33.20.0")}),-1.0]])]});
            var Q34;
            Q34=makeQuery(id+"F0.imprint","IMPRINT",FACE,{"disambiguationData":[TD([[makeQuery(id+"F0.imprint","IMPRINT",EDGE,{"derivedFrom":sQuery(id+"F0.wireOp",EDGE,"E33.11.0")}),-1.0]])]});
            var Q35;
            Q35=makeQuery(id+"F0.imprint","IMPRINT",FACE,{"disambiguationData":[TD([[makeQuery(id+"F0.imprint","IMPRINT",EDGE,{"derivedFrom":sQuery(id+"F0.wireOp",EDGE,"E33.9.0")}),-1.0]])]});
            var Q36;
            Q36=makeQuery(id+"F0.imprint","IMPRINT",FACE,{"disambiguationData":[TD([[makeQuery(id+"F0.imprint","IMPRINT",EDGE,{"derivedFrom":sQuery(id+"F0.wireOp",EDGE,"E33.8.0")}),-1.0]])]});
            var Q37;
            Q37=makeQuery(id+"F0.imprint","IMPRINT",FACE,{"disambiguationData":[TD([[makeQuery(id+"F0.imprint","IMPRINT",EDGE,{"derivedFrom":sQuery(id+"F0.wireOp",EDGE,"E33.30.0")}),-1.0]])]});
            var Q38;
            Q38=makeQuery(id+"F0.imprint","IMPRINT",FACE,{"disambiguationData":[TD([[makeQuery(id+"F0.imprint","IMPRINT",EDGE,{"derivedFrom":sQuery(id+"F0.wireOp",EDGE,"E33.31.0")}),-1.0]])]});
            var Q39;
            Q39=makeQuery(id+"F0.imprint","IMPRINT",FACE,{"disambiguationData":[TD([[makeQuery(id+"F0.imprint","IMPRINT",EDGE,{"derivedFrom":sQuery(id+"F0.wireOp",EDGE,"E33.29.0")}),-1.0]])]});
            var Q40;
            Q40=makeQuery(id+"F0.imprint","IMPRINT",FACE,{"disambiguationData":[TD([[makeQuery(id+"F0.imprint","IMPRINT",EDGE,{"derivedFrom":sQuery(id+"F0.wireOp",EDGE,"E33.28.0")}),-1.0]])]});
            var Q41;
            Q41=makeQuery(id+"F0.imprint","IMPRINT",FACE,{"disambiguationData":[TD([[makeQuery(id+"F0.imprint","IMPRINT",EDGE,{"derivedFrom":sQuery(id+"F0.wireOp",EDGE,"E33.26.0")}),-1.0]])]});
            var Q42;
            Q42=makeQuery(id+"F0.imprint","IMPRINT",FACE,{"disambiguationData":[TD([[makeQuery(id+"F0.imprint","IMPRINT",EDGE,{"derivedFrom":sQuery(id+"F0.wireOp",EDGE,"E30")}),-1.0]])]});
            var Q43;
            {var subQ0=sQuery(id+"F0.wireOp",EDGE,"E32");Q43=makeQuery(id+"F0.imprint","IMPRINT",FACE,{"disambiguationData":[TD([[makeQuery(id+"F0.imprint","IMPRINT",EDGE,{"derivedFrom":subQ0}),-1.0]])]});}
            var Q44;
            Q44=qCreatedBy(makeId("Top.planeOp"),FACE);
            extrude(context, id + "F1", {"entities" : qUnion([Q0, Q1, Q2, Q3, Q4, Q5, Q6, Q7, Q8, Q9, Q10, Q11, Q12, Q13, Q14, Q15, Q16, Q17, Q18, Q19, Q20, Q21, Q22, Q23, Q24, Q25, Q26, Q27, Q28, Q29, Q30, Q31, Q32, Q33, Q34, Q35, Q36, Q37, Q38, Q39, Q40, Q41, Q42, Q43]), "oppositeDirection" : true, "endBoundEntityFace" : qUnion([Q44]), "depth" : 25 * mm});
        }
    });
